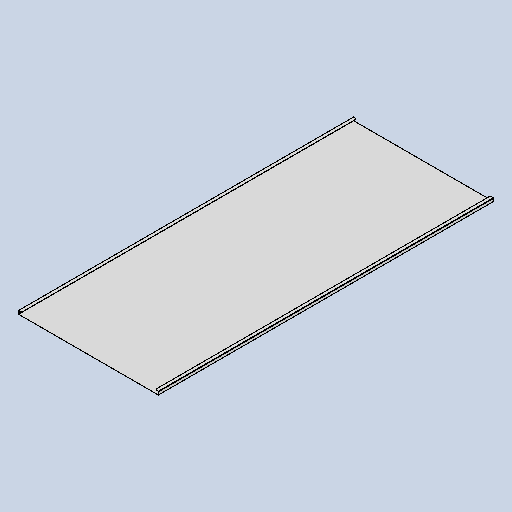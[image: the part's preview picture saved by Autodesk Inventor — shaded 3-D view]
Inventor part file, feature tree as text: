
AUTODESK INVENTOR PART (.ipt)
format: ipt  version: 2025 (Build 290162010, 162A)  size: 193,024 bytes
history: native  units: mm
features: sheet_metal_op x13, other x6, sketch x5, chamfer x1
ambient origin geometry x8: Origin, YZ Plane, XZ Plane, XY Plane, X Axis, Y Axis, Z Axis, Center Point
bodies: Body1 (feature_tree)
feature tree (25):
  sheet_metal_op  "Face1"
  sheet_metal_op  "Flange2"
  sheet_metal_op  "Flange3"
  sheet_metal_op  "Flange4"
  sheet_metal_op  "Flange5"
  chamfer  "Corner Round1"
  sketch  "Sketch6"  dims[d12=23.212879mm]
  other  "Plate2"
  sketch  "Sketch11"  dims[d52=411.0mm]
  other  "Plate4"
  sheet_metal_op  "Bend3"
  sheet_metal_op  "Corner3"
  sketch  "Sketch12"  dims[d53=980.0mm]
  other  "Plate5"
  sheet_metal_op  "Bend4"
  sheet_metal_op  "Corner4"
  sketch  "Sketch13"  dims[d54=0.5mm]
  other  "Plate6"
  sheet_metal_op  "Bend5"
  sheet_metal_op  "Corner5"
  sketch  "Sketch14"  dims[d84=0.5mm d85=0.25mm d86=1.0mm d87=0.5mm d88=10.0mm d89=90.0deg d90=0.5mm d91=2.0mm d92=0.5mm d93=0.5mm d94=0.5mm d95=0.25mm d96=1.0mm d97=0.5mm d98=10.0mm d99=90.0deg d100=0.5mm d101=2.0mm d102=0.5mm d103=0.5mm d104=0.5mm d105=0.25mm d106=1.0mm d107=0.5mm d108=10.0mm d109=90.0deg d110=0.5mm d111=2.0mm d112=0.5mm d113=0.5mm d114=0.5mm d115=0.25mm d116=1.0mm d117=0.5mm d118=10.0mm d119=90.0deg d120=0.5mm d121=2.0mm d122=0.5mm d123=0.5mm d124=4.0mm]
  other  "Plate7"
  sheet_metal_op  "Bend6"
  sheet_metal_op  "Corner6"
  other  "Definition1"
